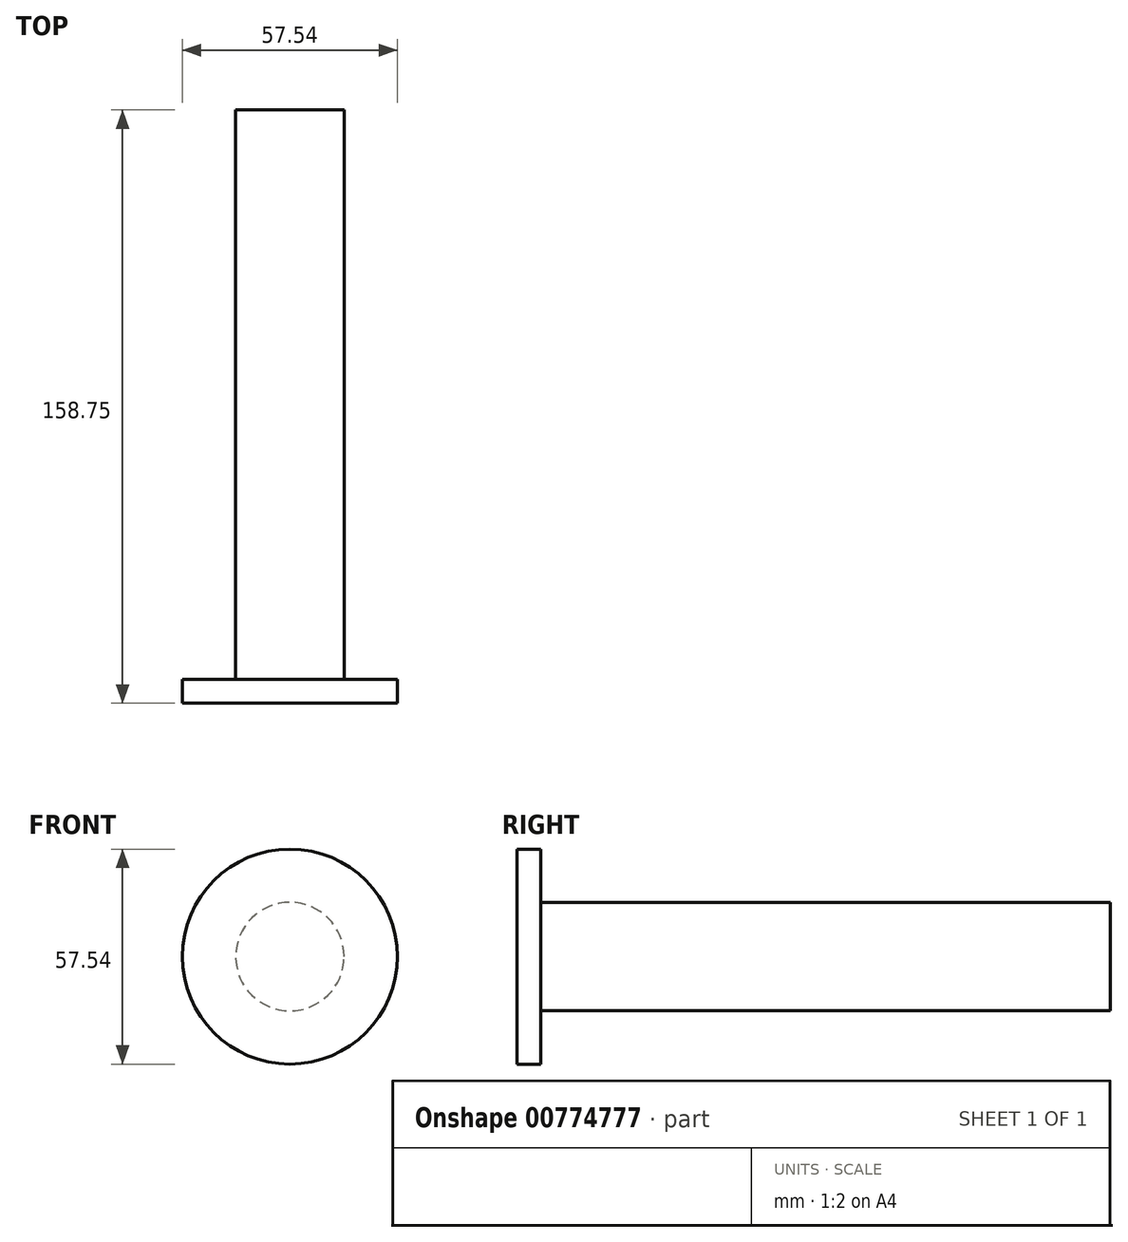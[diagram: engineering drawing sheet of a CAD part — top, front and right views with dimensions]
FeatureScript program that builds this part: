
annotation { "Feature Type Name" : "Feature", "Feature Type Description" : "" }
export const myFeature = defineFeature(function(context is Context, id is Id, definition is map)
    precondition{}
    {
        {
            var Q0;
            Q0=qCreatedBy(makeId("Front.planeOp"),FACE);
            var sketch = newSketch(context, id + "F0", { "sketchPlane" : qUnion([Q0])});
            skCircle(sketch, "E0", {"center": v(0, 0) * mm, "radius": 14.5 * mm});
            skSolve(sketch);
        }
        {
            var Q0;
            Q0=makeQuery(id+"F0.imprint","IMPRINT",FACE,{"disambiguationData":[TD([[makeQuery(id+"F0.imprint","IMPRINT",EDGE,{"derivedFrom":sQuery(id+"F0.wireOp",EDGE,"E0")}),1.0]])]});
            var Q1;
            Q1=sQuery(id+"F0.wireOp",EDGE,"E0");
            extrude(context, id + "F1", {"entities" : qUnion([Q0]), "surfaceEntities" : qUnion([Q1]), "depth" : 152.4 * mm, "offsetDistance" : 25.4 * mm});
        }
        {
            var Q0;
            Q0=makeQuery(id+"F1.opExtrude","CAP_FACE",FACE,{"disambiguationData":[OSD([sQuery(id+"F0.wireOp",EDGE,"E0")])],"isStart":false});
            var sketch = newSketch(context, id + "F2", { "sketchPlane" : qUnion([Q0])});
            skCircle(sketch, "E1", {"center": v(0, 0) * mm, "radius": 28.77 * mm});
            skSolve(sketch);
        }
        {
            var Q0;
            Q0 = qSketchRegion(id + "F2", true);
            extrude(context, id + "F3", {"entities" : qUnion([Q0]), "operationType" : NewBodyOperationType.ADD, "depth" : 6.35 * mm, "offsetDistance" : 25.4 * mm});
        }
    });
